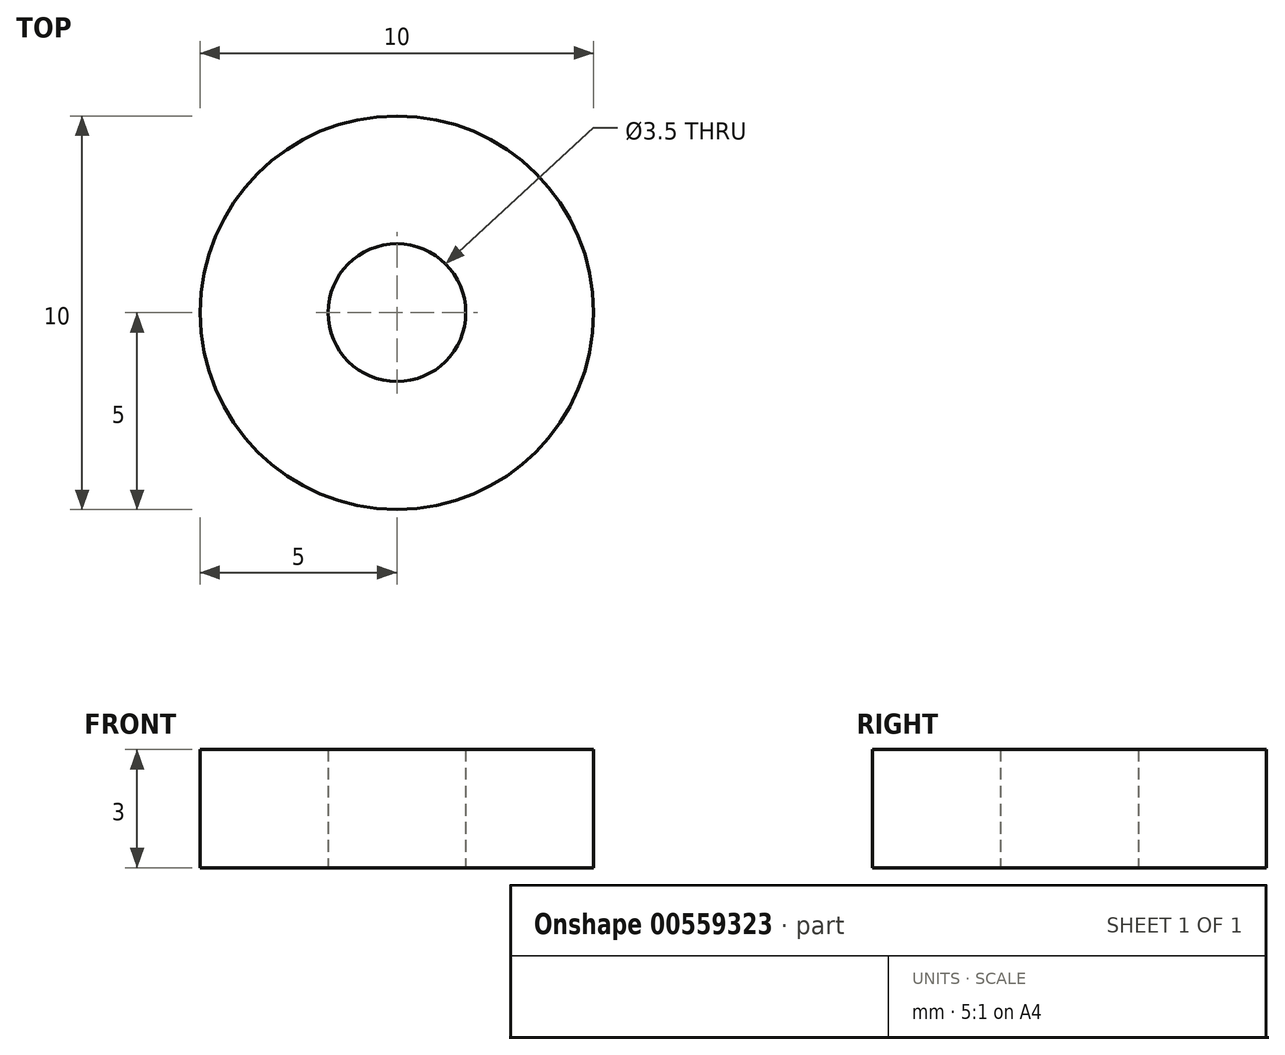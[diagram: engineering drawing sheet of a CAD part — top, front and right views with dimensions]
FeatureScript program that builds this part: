
annotation { "Feature Type Name" : "Feature", "Feature Type Description" : "" }
export const myFeature = defineFeature(function(context is Context, id is Id, definition is map)
    precondition{}
    {
        {
            var Q0;
            Q0=qCreatedBy(makeId("Top.planeOp"),FACE);
            var sketch = newSketch(context, id + "F0", { "sketchPlane" : qUnion([Q0])});
            skCircle(sketch, "E0", {"center": v(0, 0) * mm, "radius": 1.75 * mm});
            skCircle(sketch, "E1", {"center": v(0, 0) * mm, "radius": 5 * mm});
            skSolve(sketch);
        }
        {
            var Q0;
            Q0=makeQuery(id+"F0.imprint","IMPRINT",FACE,{"disambiguationData":[TD([[makeQuery(id+"F0.imprint","IMPRINT",EDGE,{"derivedFrom":sQuery(id+"F0.wireOp",EDGE,"E0")}),-1.0]])]});
            extrude(context, id + "F1", {"entities" : qUnion([Q0]), "depth" : 3 * mm, "offsetDistance" : 25 * mm});
        }
    });
